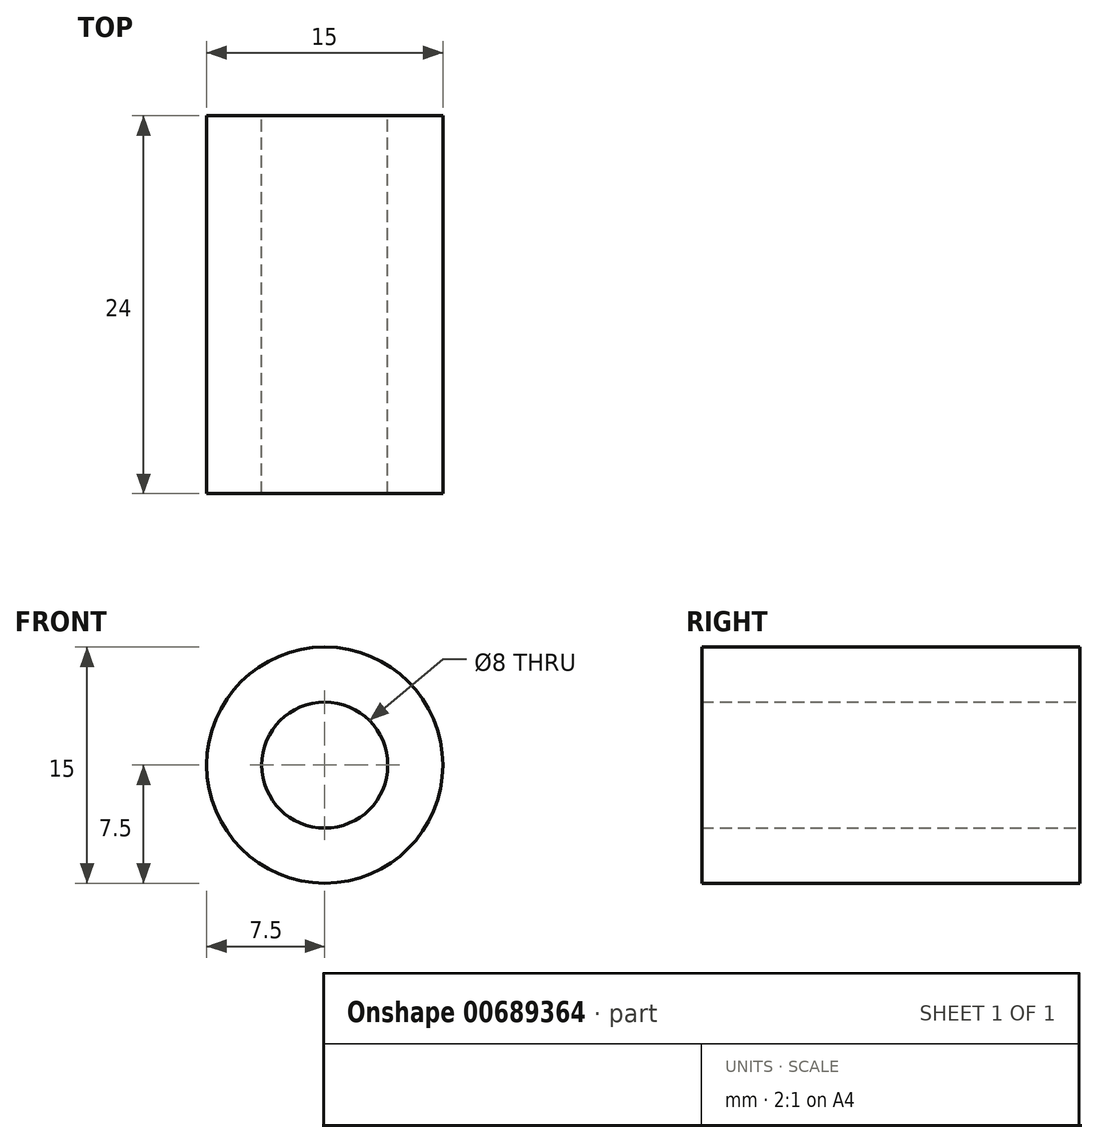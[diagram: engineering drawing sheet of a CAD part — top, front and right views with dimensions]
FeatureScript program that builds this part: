
annotation { "Feature Type Name" : "Feature", "Feature Type Description" : "" }
export const myFeature = defineFeature(function(context is Context, id is Id, definition is map)
    precondition{}
    {
        {
            var Q0;
            Q0=qCreatedBy(makeId("Front.planeOp"),FACE);
            var sketch = newSketch(context, id + "F0", { "sketchPlane" : qUnion([Q0])});
            skCircle(sketch, "E0", {"center": v(0, 0) * mm, "radius": 7.5 * mm});
            skCircle(sketch, "E1", {"center": v(0, 0) * mm, "radius": 4 * mm});
            skSolve(sketch);
        }
        {
            var Q0;
            Q0=qSketchRegion(id+"F0",true);
            extrude(context, id + "F1", {"entities" : qUnion([Q0]), "depth" : 24 * mm});
        }
    });
